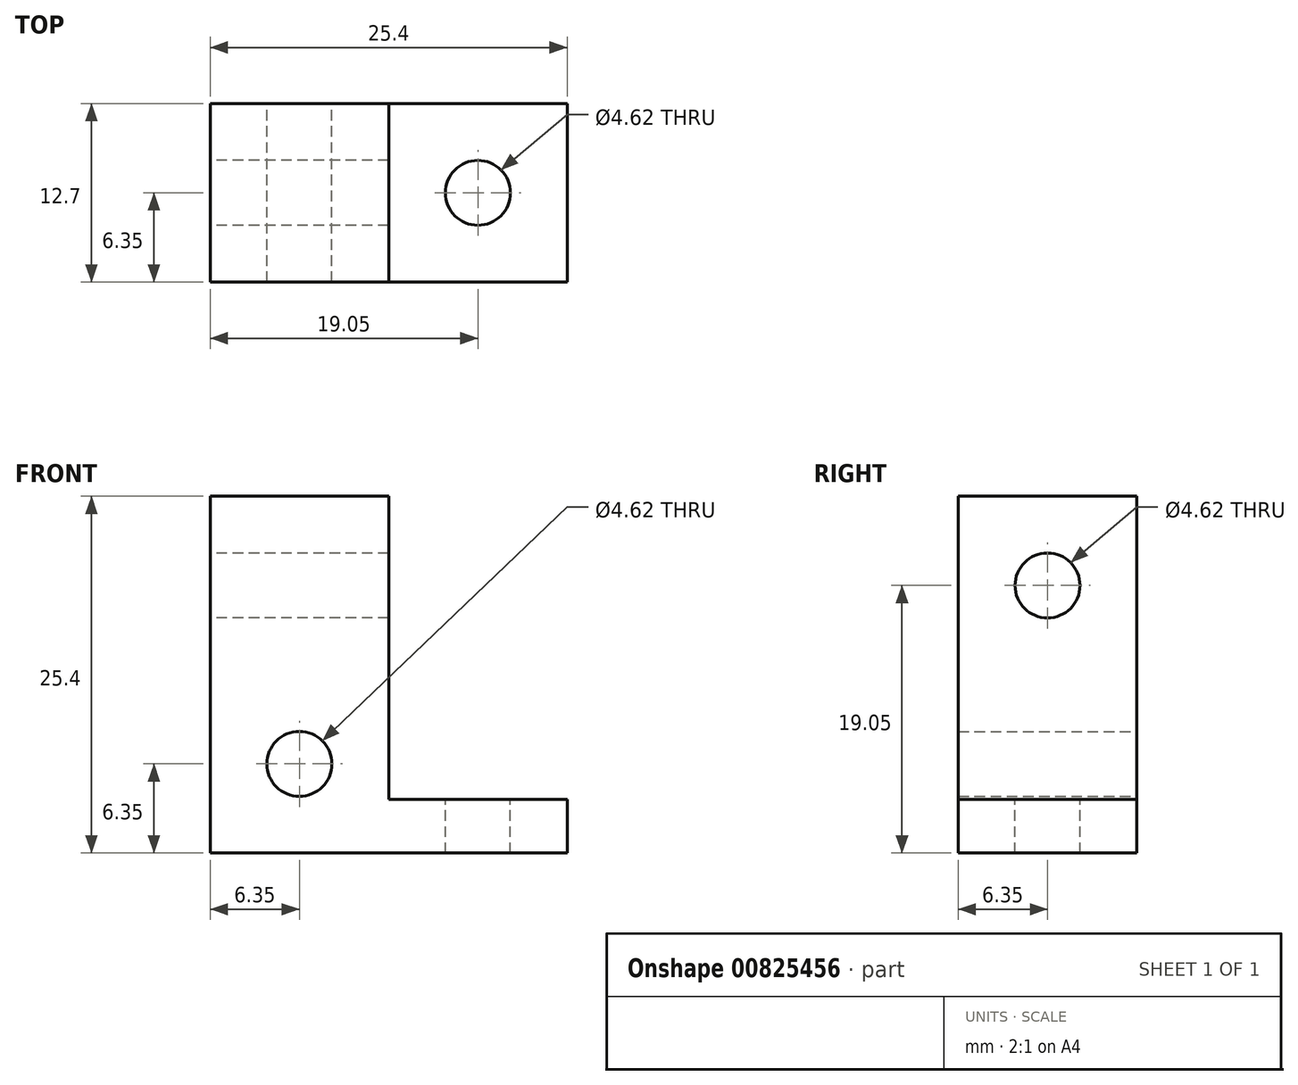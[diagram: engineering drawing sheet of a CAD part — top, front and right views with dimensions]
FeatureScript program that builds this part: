
annotation { "Feature Type Name" : "Feature", "Feature Type Description" : "" }
export const myFeature = defineFeature(function(context is Context, id is Id, definition is map)
    precondition{}
    {
        {
            var Q0;
            Q0=qCreatedBy(makeId("Front.planeOp"),FACE);
            var sketch = newSketch(context, id + "F0", { "sketchPlane" : qUnion([Q0])});
            skLineSegment(sketch, "E0", {"start": v(0, 0) * mm, "end": v(25.4, 0) * mm});
            skLineSegment(sketch, "E1", {"start": v(12.7, 3.8) * mm, "end": v(12.7, 25.4) * mm});
            skLineSegment(sketch, "E2", {"start": v(0, 0) * mm, "end": v(0, 25.4) * mm});
            skLineSegment(sketch, "E3", {"start": v(0, 25.4) * mm, "end": v(12.7, 25.4) * mm});
            skLineSegment(sketch, "E4", {"start": v(25.4, 0) * mm, "end": v(25.4, 3.8) * mm});
            skLineSegment(sketch, "E5", {"start": v(25.4, 3.8) * mm, "end": v(12.7, 3.8) * mm});
            skPoint(sketch, "E6.orphan", {"position": v(12.7, 0) * mm});
            skCircle(sketch, "E7", {"center": v(6.35, 6.35) * mm, "radius": 2.31 * mm});
            skSolve(sketch);
        }
        {
            var Q0;
            Q0 = qSketchRegion(id + "F0", true);
            extrude(context, id + "F1", {"entities" : qUnion([Q0]), "depth" : 12.7 * mm, "offsetDistance" : 25.4 * mm});
        }
        {
            var Q0;
            Q0=makeQuery(id+"F1.opExtrude","SWEPT_FACE",FACE,{"disambiguationData":[OSD([sQuery(id+"F0.wireOp",EDGE,"E2")])]});
            var sketch = newSketch(context, id + "F2", { "sketchPlane" : qUnion([Q0])});
            skCircle(sketch, "E8", {"center": v(6.35, 19.05) * mm, "radius": 2.31 * mm});
            skSolve(sketch);
        }
        {
            var Q0;
            Q0 = qSketchRegion(id + "F2", true);
            extrude(context, id + "F3", {"entities" : qUnion([Q0]), "operationType" : NewBodyOperationType.REMOVE, "oppositeDirection" : true, "depth" : 25.4 * mm, "offsetDistance" : 25.4 * mm});
        }
        {
            var Q0;
            Q0=makeQuery(id+"F1.opExtrude","SWEPT_FACE",FACE,{"disambiguationData":[OSD([sQuery(id+"F0.wireOp",EDGE,"E5")])]});
            var sketch = newSketch(context, id + "F4", { "sketchPlane" : qUnion([Q0])});
            skCircle(sketch, "E9", {"center": v(19.05, -6.35) * mm, "radius": 2.31 * mm});
            skSolve(sketch);
        }
        {
            var Q0;
            Q0 = qSketchRegion(id + "F4", true);
            extrude(context, id + "F5", {"entities" : qUnion([Q0]), "operationType" : NewBodyOperationType.REMOVE, "oppositeDirection" : true, "depth" : 3.8 * mm, "offsetDistance" : 25.4 * mm});
        }
    });
